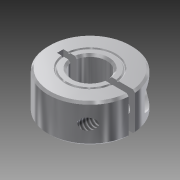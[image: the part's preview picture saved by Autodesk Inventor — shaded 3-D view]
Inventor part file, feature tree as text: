
AUTODESK INVENTOR PART (.ipt)
format: ipt  version: 2014 (Build 180170000, 170)  size: 406,016 bytes
history: native  units: mm
features: sketch x3, hole x2, other x2, surface_op x1, thread x1, extrude x1, projected_geometry x1
ambient origin geometry x8: Origin, YZ Plane, XZ Plane, XY Plane, X Axis, Y Axis, Z Axis, Center Point
bodies: Solid1 (feature_tree)
feature tree (11):
  surface_op  "Stitch Surface1"
  thread  "Thread1"  [1 undecoded]
  hole  "Hole1"  [1 undecoded]
  extrude  "Extrusion1"  [1 undecoded]
  hole  "Hole2"  [1 undecoded]
  sketch  "Sketch2"  dims[d2=3.264mm d3=6.0mm d4=9.525mm d5=1.524mm d6=14.3117mm d7=8.0mm d8=20.594885mm d9=10.0mm d10=0.0mm]
  sketch  "Sketch3"  dims[d11=2.156mm d12=6.0mm d13=9.525mm d14=1.524mm d15=14.3117mm d16=8.0mm d17=20.594885mm]
  sketch  "Sketch4"
  projected_geometry  "Projected Loop1"
  other  "Composite1"
  other  "Srf1"
note: 4 required parameter values undecoded (feature->parameter linkage not recoverable at this tier; creation-order binding heuristic only, values carry confidence <= 0.55)
